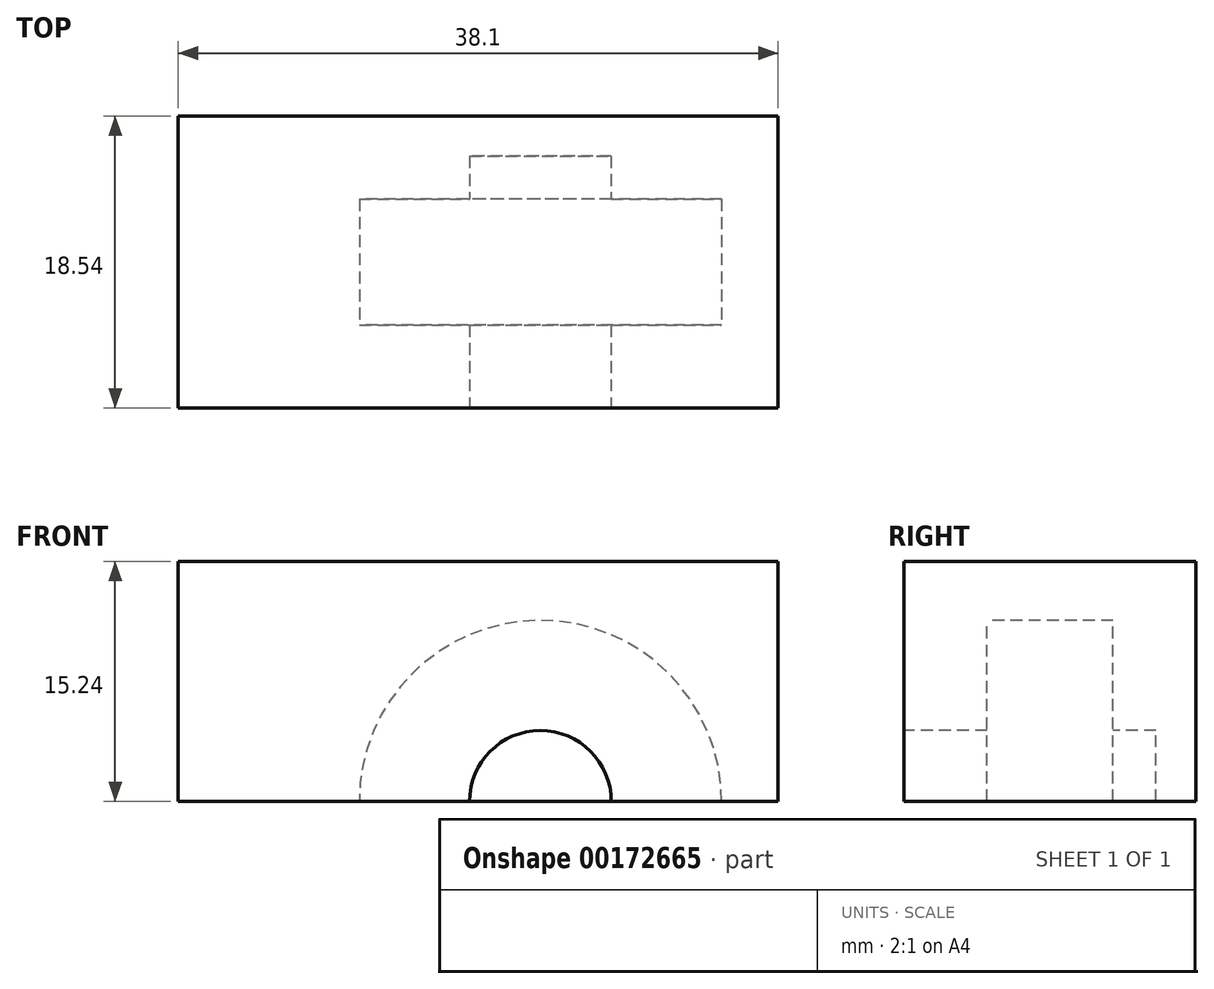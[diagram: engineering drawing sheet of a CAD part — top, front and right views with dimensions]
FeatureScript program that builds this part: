
annotation { "Feature Type Name" : "Feature", "Feature Type Description" : "" }
export const myFeature = defineFeature(function(context is Context, id is Id, definition is map)
    precondition{}
    {
        {
            var Q0;
            Q0=qCreatedBy(makeId("Top.planeOp"),FACE);
            var sketch = newSketch(context, id + "F0", { "sketchPlane" : qUnion([Q0])});
            skLineSegment(sketch, "E0.bottom", {"start": v(19.05, 9.27) * mm, "end": v(-19.05, 9.27) * mm});
            skLineSegment(sketch, "E0.top", {"start": v(19.05, -9.27) * mm, "end": v(-19.05, -9.27) * mm});
            skLineSegment(sketch, "E0.left", {"start": v(19.05, 9.27) * mm, "end": v(19.05, -9.27) * mm});
            skLineSegment(sketch, "E0.right", {"start": v(-19.05, 9.27) * mm, "end": v(-19.05, -9.27) * mm});
            skPoint(sketch, "E0.middle", {"position": v(0, 0) * mm});
            skLineSegment(sketch, "E1", {"start": v(-19.05, 0) * mm, "end": v(19.05, 0) * mm, "construction": true});
            skLineSegment(sketch, "E2", {"start": v(-19.05, -4) * mm, "end": v(19.05, -4) * mm});
            skSolve(sketch);
        }
        {
            var Q0;
            {var subQ0=sQuery(id+"F0.wireOp",EDGE,"E0.bottom");Q0=makeQuery(id+"F0.imprint","IMPRINT",FACE,{"disambiguationData":[TD([[makeQuery(id+"F0.imprint","IMPRINT",EDGE,{"derivedFrom":subQ0}),1.0]])]});}
            extrude(context, id + "F1", {"entities" : qUnion([Q0]), "depth" : 15.24 * mm});
        }
        {
            var Q0;
            Q0=makeQuery(id+"F1.opExtrude","SWEPT_FACE",FACE,{"disambiguationData":[OSD([sQuery(id+"F0.wireOp",EDGE,"E2")])]});
            var sketch = newSketch(context, id + "F2", { "sketchPlane" : qUnion([Q0])});
            skCircle(sketch, "E3", {"center": v(3.95, 0) * mm, "radius": 11.5 * mm});
            skCircle(sketch, "E4", {"center": v(3.95, 0) * mm, "radius": 4.5 * mm});
            skSolve(sketch);
        }
        {
            var Q0;
            {var subQ0=sQuery(id+"F2.wireOp",EDGE,"E3");var subQ1=makeQuery(id+"F1.opExtrude","CAP_EDGE",EDGE,{"disambiguationData":[OSD([sQuery(id+"F0.wireOp",EDGE,"E2")])],"isStart":true});var subQ2=makeQuery(id+"F2.imprint","INTERSECT",VERTEX,{"disambiguationData":[OD(0.0)],"derivedFrom":[subQ1,subQ0]});Q0=makeQuery(id+"F2.imprint","IMPRINT",FACE,{"disambiguationData":[TD([[makeQuery(id+"F2.imprint","IMPRINT",EDGE,{"disambiguationData":[TD([[subQ2,1.0]])],"derivedFrom":subQ0}),1.0]])]});}
            var Q1;
            {var subQ0=sQuery(id+"F2.wireOp",EDGE,"E4");var subQ1=makeQuery(id+"F1.opExtrude","CAP_EDGE",EDGE,{"disambiguationData":[OSD([sQuery(id+"F0.wireOp",EDGE,"E2")])],"isStart":true});var subQ2=makeQuery(id+"F2.imprint","INTERSECT",VERTEX,{"disambiguationData":[OD(0.0)],"derivedFrom":[subQ1,subQ0]});Q1=makeQuery(id+"F2.imprint","IMPRINT",FACE,{"disambiguationData":[TD([[makeQuery(id+"F2.imprint","IMPRINT",EDGE,{"disambiguationData":[TD([[subQ2,1.0]])],"derivedFrom":subQ0}),1.0]])]});}
            extrude(context, id + "F3", {"entities" : qUnion([Q0, Q1]), "operationType" : NewBodyOperationType.REMOVE, "oppositeDirection" : true, "depth" : 8 * mm});
        }
        {
            var Q0;
            {var subQ0=sQuery(id+"F0.wireOp",EDGE,"E0.top");Q0=makeQuery(id+"F0.imprint","IMPRINT",FACE,{"disambiguationData":[TD([[makeQuery(id+"F0.imprint","IMPRINT",EDGE,{"derivedFrom":subQ0}),-1.0]])]});}
            extrude(context, id + "F4", {"entities" : qUnion([Q0]), "operationType" : NewBodyOperationType.ADD, "depth" : 15.24 * mm});
        }
        {
            var Q0;
            Q0=makeQuery(id+"F4.opExtrude","SWEPT_FACE",FACE,{"disambiguationData":[OSD([sQuery(id+"F0.wireOp",EDGE,"E0.top")])]});
            var sketch = newSketch(context, id + "F5", { "sketchPlane" : qUnion([Q0])});
            skCircle(sketch, "E5", {"center": v(3.95, 0) * mm, "radius": 4.5 * mm});
            skSolve(sketch);
        }
        {
            var Q0;
            Q0=qSketchRegion(id+"F5",true);
            extrude(context, id + "F6", {"entities" : qUnion([Q0]), "operationType" : NewBodyOperationType.REMOVE, "oppositeDirection" : true, "depth" : 16 * mm});
        }
    });
